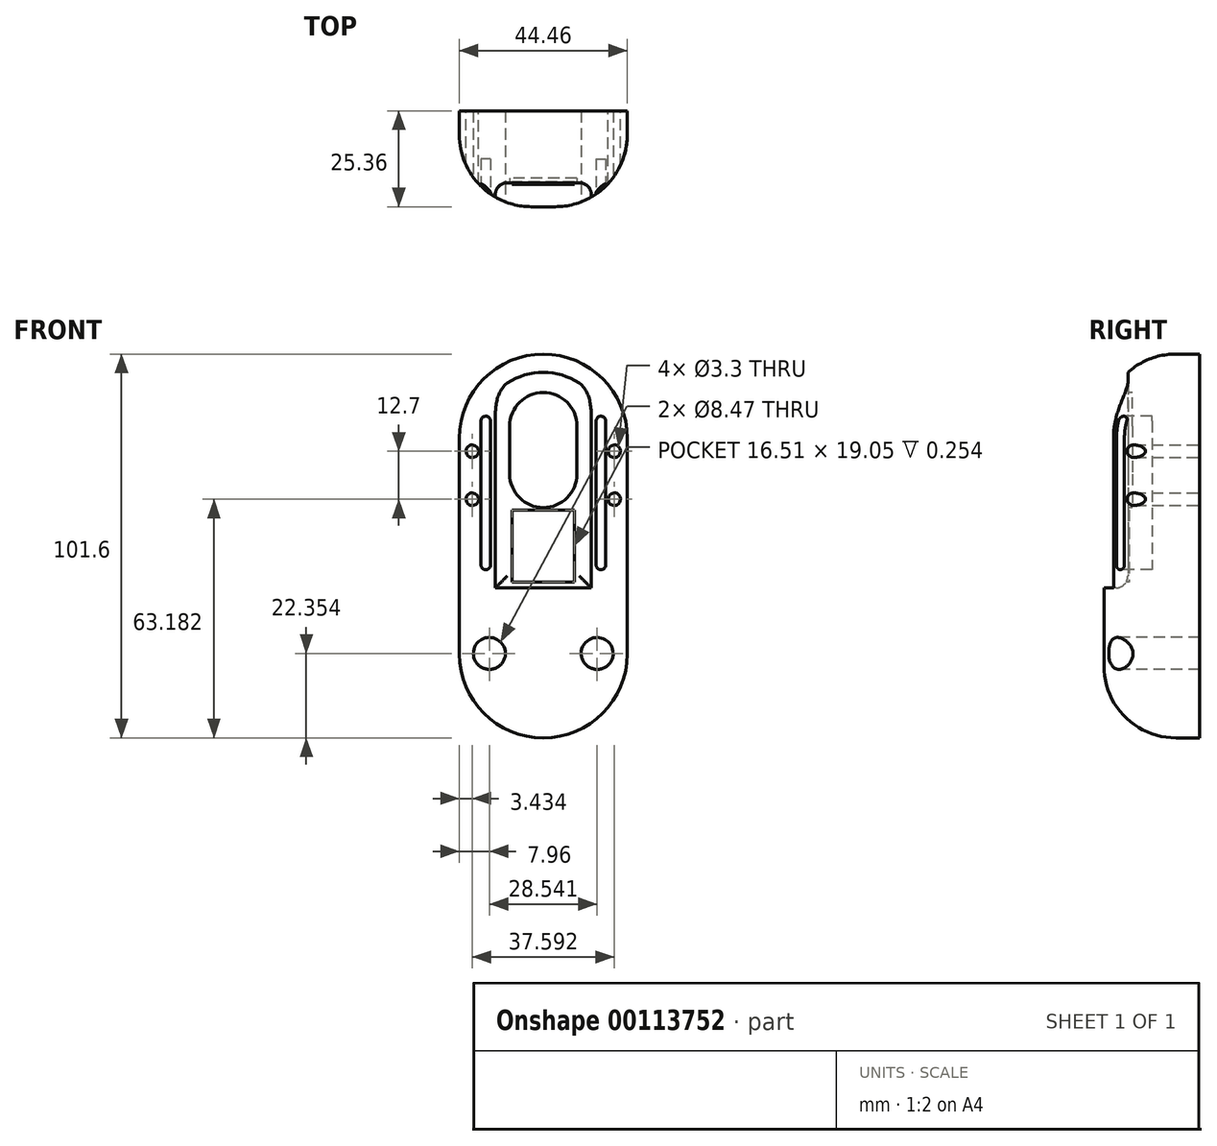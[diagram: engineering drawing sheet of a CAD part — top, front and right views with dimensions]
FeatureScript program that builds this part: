
annotation { "Feature Type Name" : "Feature", "Feature Type Description" : "" }
export const myFeature = defineFeature(function(context is Context, id is Id, definition is map)
    precondition{}
    {
        {
            var Q0;
            Q0=qCreatedBy(makeId("Front.planeOp"),FACE);
            var sketch = newSketch(context, id + "F0", { "sketchPlane" : qUnion([Q0])});
            skLineSegment(sketch, "E0.bottom", {"start": v(25.4, 50.8) * mm, "end": v(-25.4, 50.8) * mm});
            skLineSegment(sketch, "E0.top", {"start": v(25.4, -50.8) * mm, "end": v(-25.4, -50.8) * mm});
            skLineSegment(sketch, "E0.left", {"start": v(25.4, 50.8) * mm, "end": v(25.4, -50.8) * mm});
            skLineSegment(sketch, "E0.right", {"start": v(-25.4, 50.8) * mm, "end": v(-25.4, -50.8) * mm});
            skPoint(sketch, "E0.middle", {"position": v(0, 0) * mm});
            skSolve(sketch);
        }
        {
            var Q0;
            Q0=qSketchRegion(id+"F0",true);
            extrude(context, id + "F1", {"entities" : qUnion([Q0]), "depth" : 12.7 * mm});
        }
        {
            var Q0;
            Q0=qCreatedBy(makeId("Front.planeOp"),FACE);
            cPlane(context, id + "F2", {"entities" : qUnion([Q0]), "cplaneType" : CPlaneType.OFFSET, "offset" : 12.7 * mm, "width" : 152.4 * mm, "height" : 152.4 * mm});
        }
        {
            var Q0;
            Q0=qCreatedBy(id+"F2.planeOp",FACE);
            var sketch = newSketch(context, id + "F3", { "sketchPlane" : qUnion([Q0])});
            skLineSegment(sketch, "E1.bottom", {"start": v(22.23, 28.57) * mm, "end": v(-22.22, 28.57) * mm});
            skLineSegment(sketch, "E1.top", {"start": v(22.22, -28.58) * mm, "end": v(-22.22, -28.58) * mm});
            skLineSegment(sketch, "E1.left", {"start": v(22.22, 28.57) * mm, "end": v(22.22, -28.58) * mm});
            skLineSegment(sketch, "E1.right", {"start": v(-22.23, 28.57) * mm, "end": v(-22.23, -28.58) * mm});
            skPoint(sketch, "E1.middle", {"position": v(0, 0) * mm});
            skArc(sketch, "E2", {"start": v(22.23, 28.58) * mm, "mid": v(0, 50.8) * mm, "end": v(-22.23, 28.57) * mm});
            skArc(sketch, "E3", {"start": v(-22.23, -28.58) * mm, "mid": v(0, -50.8) * mm, "end": v(22.23, -28.58) * mm});
            skSolve(sketch);
        }
        {
            var Q0;
            Q0=qSketchRegion(id+"F3",true);
            extrude(context, id + "F4", {"entities" : qUnion([Q0]), "operationType" : NewBodyOperationType.ADD, "depth" : 25.4 * mm});
        }
        {
            var Q0;
            Q0=makeQuery(id+"F4.opExtrude","CAP_EDGE",EDGE,{"disambiguationData":[OSD([sQuery(id+"F3.wireOp",EDGE,"E1.left")])],"isStart":false});
            fillet(context, id + "F5", {"entities" : qUnion([Q0]), "radius" : 19.05 * mm, "tangentPropagation" : true, "allowEdgeOverflow" : false});
        }
        {
            var Q0;
            Q0=makeQuery(id+"F4.opExtrude","CAP_FACE",FACE,{"disambiguationData":[OSD([sQuery(id+"F3.wireOp",EDGE,"E1.left"),sQuery(id+"F3.wireOp",EDGE,"E1.right"),sQuery(id+"F3.wireOp",EDGE,"E2"),sQuery(id+"F3.wireOp",EDGE,"E3")])],"isStart":false});
            var sketch = newSketch(context, id + "F6", { "sketchPlane" : qUnion([Q0])});
            skLineSegment(sketch, "E4.left", {"start": v(12.7, 103.58) * mm, "end": v(12.7, 7.15) * mm});
            skLineSegment(sketch, "E4.right", {"start": v(-12.7, 103.58) * mm, "end": v(-12.7, 7.15) * mm});
            skPoint(sketch, "E5.middle", {"position": v(0, 31.75) * mm});
            skLineSegment(sketch, "E6", {"start": v(-12.7, 103.58) * mm, "end": v(12.7, 103.58) * mm});
            skPoint(sketch, "E7.orphan", {"position": v(-12.7, 56.35) * mm});
            skPoint(sketch, "E8.orphan", {"position": v(12.7, 56.35) * mm});
            skLineSegment(sketch, "E9.top", {"start": v(-12.7, -11.11) * mm, "end": v(12.7, -11.11) * mm});
            skLineSegment(sketch, "E9.left", {"start": v(-12.7, 7.15) * mm, "end": v(-12.7, -11.11) * mm});
            skLineSegment(sketch, "E9.right", {"start": v(12.7, 7.15) * mm, "end": v(12.7, -11.11) * mm});
            skSolve(sketch);
        }
        {
            var Q0;
            Q0=qSketchRegion(id+"F6",true);
            extrude(context, id + "F7", {"entities" : qUnion([Q0]), "operationType" : NewBodyOperationType.REMOVE, "oppositeDirection" : true, "depth" : 6.35 * mm});
        }
        {
            var Q0;
            {var subQ0=sQuery(id+"F3.wireOp",EDGE,"E1.left");var subQ1=sQuery(id+"F3.wireOp",EDGE,"E1.right");var subQ2=sQuery(id+"F3.wireOp",EDGE,"E3");Q0=makeQuery(id+"F7.boolean.opBoolean","SPLIT",FACE,{"disambiguationData":[TD([makeQuery(id+"F5.opFillet","BLEND_FACE",FACE,{"disambiguationData":[OSD([subQ2])]})])],"derivedFrom":makeQuery(id+"F4.opExtrude","CAP_FACE",FACE,{"disambiguationData":[OSD([subQ0,subQ1,sQuery(id+"F3.wireOp",EDGE,"E2"),subQ2])],"isStart":false})});}
            var sketch = newSketch(context, id + "F8", { "sketchPlane" : qUnion([Q0])});
            skCircle(sketch, "E10", {"center": v(-14.27, -28.45) * mm, "radius": 4.23 * mm});
            skCircle(sketch, "E11.MirrorC", {"center": v(14.27, -28.45) * mm, "radius": 4.23 * mm});
            skSolve(sketch);
        }
        {
            var Q0;
            Q0=qSketchRegion(id+"F8",true);
            extrude(context, id + "F9", {"entities" : qUnion([Q0]), "operationType" : NewBodyOperationType.REMOVE, "oppositeDirection" : true, "depth" : 25.4 * mm});
        }
        {
            var Q0;
            {var subQ0=sQuery(id+"F3.wireOp",EDGE,"E1.left");var subQ1=sQuery(id+"F3.wireOp",EDGE,"E1.right");var subQ2=sQuery(id+"F3.wireOp",EDGE,"E3");Q0=makeQuery(id+"F7.boolean.opBoolean","SPLIT",FACE,{"disambiguationData":[TD([makeQuery(id+"F5.opFillet","BLEND_FACE",FACE,{"disambiguationData":[OSD([subQ2])]})])],"derivedFrom":makeQuery(id+"F4.opExtrude","CAP_FACE",FACE,{"disambiguationData":[OSD([subQ0,subQ1,sQuery(id+"F3.wireOp",EDGE,"E2"),subQ2])],"isStart":false})});}
            var sketch = newSketch(context, id + "F10", { "sketchPlane" : qUnion([Q0])});
            skLineSegment(sketch, "E12.left", {"start": v(-16.5, 33.08) * mm, "end": v(-16.5, -5.02) * mm});
            skLineSegment(sketch, "E12.right", {"start": v(-13.97, 33.08) * mm, "end": v(-13.97, -5.02) * mm});
            skArc(sketch, "E13", {"start": v(-13.97, 33.08) * mm, "mid": v(-15.24, 34.35) * mm, "end": v(-16.5, 33.08) * mm});
            skArc(sketch, "E14", {"start": v(-16.5, -5.02) * mm, "mid": v(-15.24, -6.3) * mm, "end": v(-13.97, -5.02) * mm});
            skLineSegment(sketch, "E15.MirrorCS", {"start": v(16.5, 33.08) * mm, "end": v(16.5, -5.02) * mm});
            skLineSegment(sketch, "E16.MirrorCS", {"start": v(13.97, 33.08) * mm, "end": v(13.97, -5.02) * mm});
            skArc(sketch, "E17.MirrorCS", {"start": v(16.5, -5.02) * mm, "mid": v(15.24, -6.3) * mm, "end": v(13.97, -5.02) * mm});
            skArc(sketch, "E18.MirrorCS", {"start": v(13.97, 33.08) * mm, "mid": v(15.24, 34.35) * mm, "end": v(16.5, 33.08) * mm});
            skSolve(sketch);
        }
        {
            var Q0;
            Q0=qSketchRegion(id+"F10",true);
            extrude(context, id + "F11", {"entities" : qUnion([Q0]), "operationType" : NewBodyOperationType.REMOVE, "oppositeDirection" : true, "depth" : 12.7 * mm});
        }
        {
            var Q0;
            Q0=qCreatedBy(makeId("Top.planeOp"),FACE);
            cPlane(context, id + "F12", {"entities" : qUnion([Q0]), "cplaneType" : CPlaneType.OFFSET, "offset" : 28.57 * mm, "width" : 152.4 * mm, "height" : 152.4 * mm});
        }
        {
            var Q0;
            Q0=makeQuery(id+"F7.boolean.opBoolean","COPY",EDGE,{"derivedFrom":makeQuery(id+"F7.opExtrude","CAP_EDGE",EDGE,{"disambiguationData":[OSD([sQuery(id+"F6.wireOp",EDGE,"E4.left"),sQuery(id+"F6.wireOp",EDGE,"E9.right")])],"isStart":false})});
            var Q1;
            Q1=makeQuery(id+"F7.boolean.opBoolean","COPY",EDGE,{"derivedFrom":makeQuery(id+"F7.opExtrude","CAP_EDGE",EDGE,{"disambiguationData":[OSD([sQuery(id+"F6.wireOp",EDGE,"E4.right"),sQuery(id+"F6.wireOp",EDGE,"E9.left")])],"isStart":false})});
            var Q2;
            Q2=makeQuery(id+"F7.boolean.opBoolean","COPY",EDGE,{"derivedFrom":makeQuery(id+"F7.opExtrude","CAP_EDGE",EDGE,{"disambiguationData":[OSD([sQuery(id+"F6.wireOp",EDGE,"E9.top")])],"isStart":false})});
            fillet(context, id + "F13", {"entities" : qUnion([Q0, Q1, Q2]), "radius" : 3.17 * mm, "tangentPropagation" : true, "allowEdgeOverflow" : false});
        }
        {
            var Q0;
            Q0=qCreatedBy(makeId("Top.planeOp"),FACE);
            var sketch = newSketch(context, id + "F14", { "sketchPlane" : qUnion([Q0])});
            skCircle(sketch, "E19", {"center": v(-0.3, 165.55) * mm, "radius": 168.33 * mm});
            skPoint(sketch, "E19.first.point", {"position": v(-30.78, 0) * mm});
            skPoint(sketch, "E19.second.point", {"position": v(30.2, 0) * mm});
            skPoint(sketch, "E19.third.point", {"position": v(13.86, -2.19) * mm});
            skSolve(sketch);
        }
        {
            var Q0;
            Q0=qSketchRegion(id+"F14",true);
            extrude(context, id + "F15", {"entities" : qUnion([Q0]), "operationType" : NewBodyOperationType.REMOVE, "depth" : 152.4 * mm, "symmetric" : true});
        }
        {
            var Q0;
            Q0=makeQuery(id+"F1.opExtrude","SWEPT_BODY",BODY,{"disambiguationData":[OSD([sQuery(id+"F0.wireOp",EDGE,"E0.bottom"),sQuery(id+"F0.wireOp",EDGE,"E0.top"),sQuery(id+"F0.wireOp",EDGE,"E0.left"),sQuery(id+"F0.wireOp",EDGE,"E0.right")])]});
            transform(context, id + "F16", {"entities" : qUnion([Q0]), "transformType" : TransformType.TRANSLATION_3D, "dx" : 0 * mm, "dy" : 0 * mm, "dz" : 0 * mm, "makeCopy" : true});
        }
        {
            var Q0;
            Q0=makeQuery(id+"F16.opPattern","COPY",BODY,{"derivedFrom":makeQuery(id+"F1.opExtrude","SWEPT_BODY",BODY,{"disambiguationData":[OSD([sQuery(id+"F0.wireOp",EDGE,"E0.bottom"),sQuery(id+"F0.wireOp",EDGE,"E0.top"),sQuery(id+"F0.wireOp",EDGE,"E0.left"),sQuery(id+"F0.wireOp",EDGE,"E0.right")])]}),"instanceName":"1"});
            deleteBodies(context, id + "F17", {"entities" : qUnion([Q0])});
        }
        {
            var Q0;
            Q0=qCreatedBy(makeId("Right.planeOp"),FACE);
            var sketch = newSketch(context, id + "F18", { "sketchPlane" : qUnion([Q0])});
            skLineSegment(sketch, "E20.bottom", {"start": v(5.64, 54.27) * mm, "end": v(-12.74, 54.27) * mm});
            skLineSegment(sketch, "E20.top", {"start": v(5.64, -63.07) * mm, "end": v(-12.74, -63.07) * mm});
            skLineSegment(sketch, "E20.left", {"start": v(5.64, 54.27) * mm, "end": v(5.64, -63.07) * mm});
            skLineSegment(sketch, "E20.right", {"start": v(-12.74, 54.27) * mm, "end": v(-12.74, -63.07) * mm});
            skSolve(sketch);
        }
        {
            var Q0;
            Q0 = qSketchRegion(id + "F18", true);
            extrude(context, id + "F19", {"entities" : qUnion([Q0]), "operationType" : NewBodyOperationType.REMOVE, "oppositeDirection" : true, "depth" : 76.2 * mm, "symmetric" : true});
        }
        {
            var Q0;
            Q0=qCreatedBy(id+"F2.planeOp",FACE);
            var sketch = newSketch(context, id + "F20", { "sketchPlane" : qUnion([Q0])});
            skCircle(sketch, "E21", {"center": v(-18.8, 25.08) * mm, "radius": 1.65 * mm});
            skCircle(sketch, "E22", {"center": v(-18.8, 12.38) * mm, "radius": 1.65 * mm});
            skCircle(sketch, "E23.MirrorC", {"center": v(18.8, 25.08) * mm, "radius": 1.65 * mm});
            skCircle(sketch, "E24.MirrorC", {"center": v(18.8, 12.38) * mm, "radius": 1.65 * mm});
            skSolve(sketch);
        }
        {
            var Q0;
            Q0 = qSketchRegion(id + "F20", true);
            extrude(context, id + "F21", {"entities" : qUnion([Q0]), "operationType" : NewBodyOperationType.REMOVE, "depth" : 25.4 * mm});
        }
        {
            var Q0;
            Q0=makeQuery(id+"F7.boolean.opBoolean","COPY",FACE,{"derivedFrom":makeQuery(id+"F7.opExtrude","CAP_FACE",FACE,{"disambiguationData":[OSD([sQuery(id+"F6.wireOp",EDGE,"E4.left"),sQuery(id+"F6.wireOp",EDGE,"E4.right"),sQuery(id+"F6.wireOp",EDGE,"E6"),sQuery(id+"F6.wireOp",EDGE,"E9.top"),sQuery(id+"F6.wireOp",EDGE,"E9.left"),sQuery(id+"F6.wireOp",EDGE,"E9.right")])],"isStart":false})});
            var sketch = newSketch(context, id + "F22", { "sketchPlane" : qUnion([Q0])});
            skLineSegment(sketch, "E25.bottom", {"start": v(8.89, 31.75) * mm, "end": v(-8.89, 31.75) * mm});
            skLineSegment(sketch, "E25.top", {"start": v(8.9, 19.05) * mm, "end": v(-8.89, 19.05) * mm});
            skLineSegment(sketch, "E25.left", {"start": v(8.9, 31.75) * mm, "end": v(8.9, 19.05) * mm});
            skLineSegment(sketch, "E25.right", {"start": v(-8.89, 31.75) * mm, "end": v(-8.89, 19.05) * mm});
            skPoint(sketch, "E25.middle", {"position": v(0, 25.4) * mm});
            skArc(sketch, "E26", {"start": v(8.89, 31.75) * mm, "mid": v(0, 40.64) * mm, "end": v(-8.9, 31.75) * mm});
            skArc(sketch, "E27", {"start": v(-8.89, 19.05) * mm, "mid": v(0, 10.16) * mm, "end": v(8.9, 19.05) * mm});
            skSolve(sketch);
        }
        {
            var Q0;
            Q0 = qSketchRegion(id + "F22", true);
            extrude(context, id + "F23", {"entities" : qUnion([Q0]), "operationType" : NewBodyOperationType.REMOVE, "oppositeDirection" : true, "depth" : 1.27 * mm});
        }
        {
            var Q0;
            Q0=makeQuery(id+"F7.boolean.opBoolean","COPY",FACE,{"derivedFrom":makeQuery(id+"F7.opExtrude","CAP_FACE",FACE,{"disambiguationData":[OSD([sQuery(id+"F6.wireOp",EDGE,"E4.left"),sQuery(id+"F6.wireOp",EDGE,"E4.right"),sQuery(id+"F6.wireOp",EDGE,"E6"),sQuery(id+"F6.wireOp",EDGE,"E9.top"),sQuery(id+"F6.wireOp",EDGE,"E9.left"),sQuery(id+"F6.wireOp",EDGE,"E9.right")])],"isStart":false})});
            var sketch = newSketch(context, id + "F24", { "sketchPlane" : qUnion([Q0])});
            skLineSegment(sketch, "E28.bottom", {"start": v(8.26, 9.53) * mm, "end": v(-8.26, 9.53) * mm});
            skLineSegment(sketch, "E28.top", {"start": v(8.26, -9.53) * mm, "end": v(-8.26, -9.53) * mm});
            skLineSegment(sketch, "E28.left", {"start": v(8.26, 9.53) * mm, "end": v(8.26, -9.53) * mm});
            skLineSegment(sketch, "E28.right", {"start": v(-8.26, 9.53) * mm, "end": v(-8.26, -9.53) * mm});
            skPoint(sketch, "E28.middle", {"position": v(0, 0) * mm});
            skSolve(sketch);
        }
        {
            var Q0;
            Q0 = qSketchRegion(id + "F24", true);
            extrude(context, id + "F25", {"entities" : qUnion([Q0]), "operationType" : NewBodyOperationType.REMOVE, "oppositeDirection" : true, "depth" : 0.25 * mm, "hasSecondDirection" : true, "secondDirectionOppositeDirection" : false, "secondDirectionDepth" : 25.4 * mm});
        }
    });
